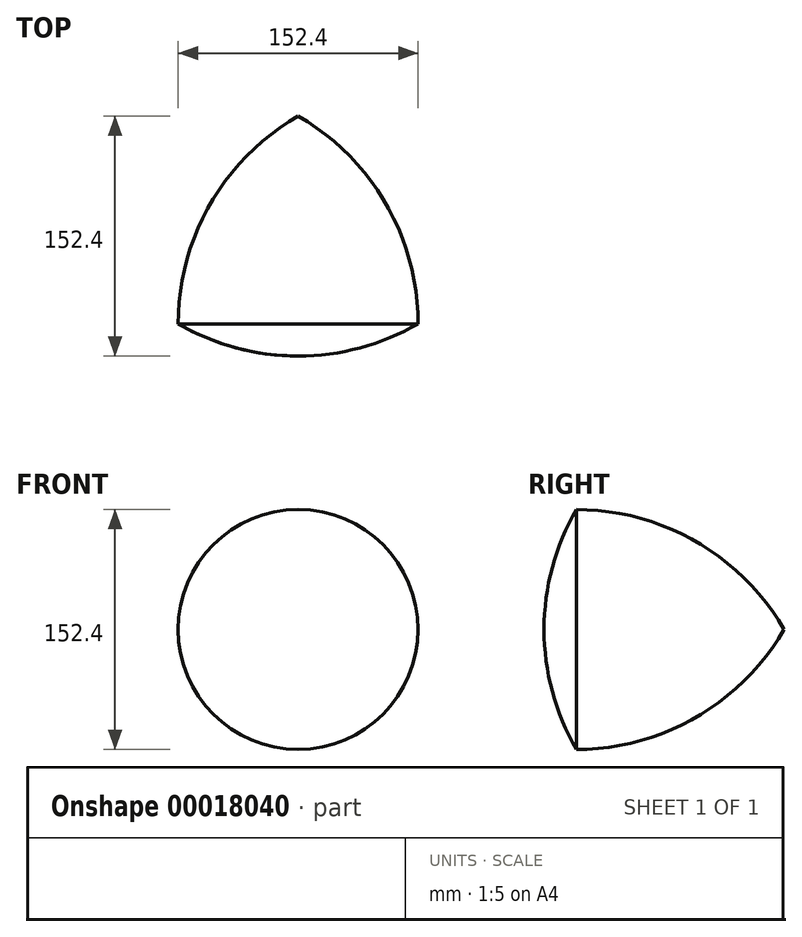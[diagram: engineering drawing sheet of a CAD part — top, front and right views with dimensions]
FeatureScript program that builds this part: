
annotation { "Feature Type Name" : "Feature", "Feature Type Description" : "" }
export const myFeature = defineFeature(function(context is Context, id is Id, definition is map)
    precondition{}
    {
        {
            var Q0;
            Q0=qCreatedBy(makeId("Top.planeOp"),FACE);
            var sketch = newSketch(context, id + "F0", { "sketchPlane" : qUnion([Q0])});
            skLineSegment(sketch, "E0", {"start": v(-76.2, 0) * mm, "end": v(76.2, 0) * mm});
            skLineSegment(sketch, "E1", {"start": v(76.2, 0) * mm, "end": v(0, 131.98) * mm});
            skLineSegment(sketch, "E2", {"start": v(0, 131.98) * mm, "end": v(-76.2, 0) * mm});
            skCircle(sketch, "E3", {"center": v(-76.2, 0) * mm, "radius": 152.4 * mm});
            skCircle(sketch, "E4", {"center": v(76.2, 0) * mm, "radius": 152.4 * mm});
            skCircle(sketch, "E5", {"center": v(0, 131.98) * mm, "radius": 152.4 * mm});
            skLineSegment(sketch, "E6", {"start": v(0, 131.98) * mm, "end": v(0, 0) * mm});
            skLineSegment(sketch, "E7", {"start": v(0, 0) * mm, "end": v(0, -20.42) * mm});
            skSolve(sketch);
        }
        {
            var Q0;
            {var subQ1=sQuery(id+"F0.wireOp",EDGE,"E1");Q0=makeQuery(id+"F0.imprint","IMPRINT",FACE,{"disambiguationData":[TD([[makeQuery(id+"F0.imprint","IMPRINT",EDGE,{"derivedFrom":subQ1}),-1.0]])]});}
            var Q1;
            {var subQ1=sQuery(id+"F0.wireOp",EDGE,"E1");Q1=makeQuery(id+"F0.imprint","IMPRINT",FACE,{"disambiguationData":[TD([[makeQuery(id+"F0.imprint","IMPRINT",EDGE,{"derivedFrom":subQ1}),1.0]])]});}
            var Q2;
            {var subQ0=sQuery(id+"F0.wireOp",EDGE,"E7");Q2=makeQuery(id+"F0.imprint","IMPRINT",FACE,{"disambiguationData":[TD([[makeQuery(id+"F0.imprint","IMPRINT",EDGE,{"derivedFrom":subQ0}),1.0]])]});}
            var Q3;
            Q3=sQuery(id+"F0.wireOp",EDGE,"E6");
            revolve(context, id + "F1", {"entities" : qUnion([Q0, Q1, Q2]), "axis" : qUnion([Q3]), "revolveType" : RevolveType.FULL});
        }
    });
